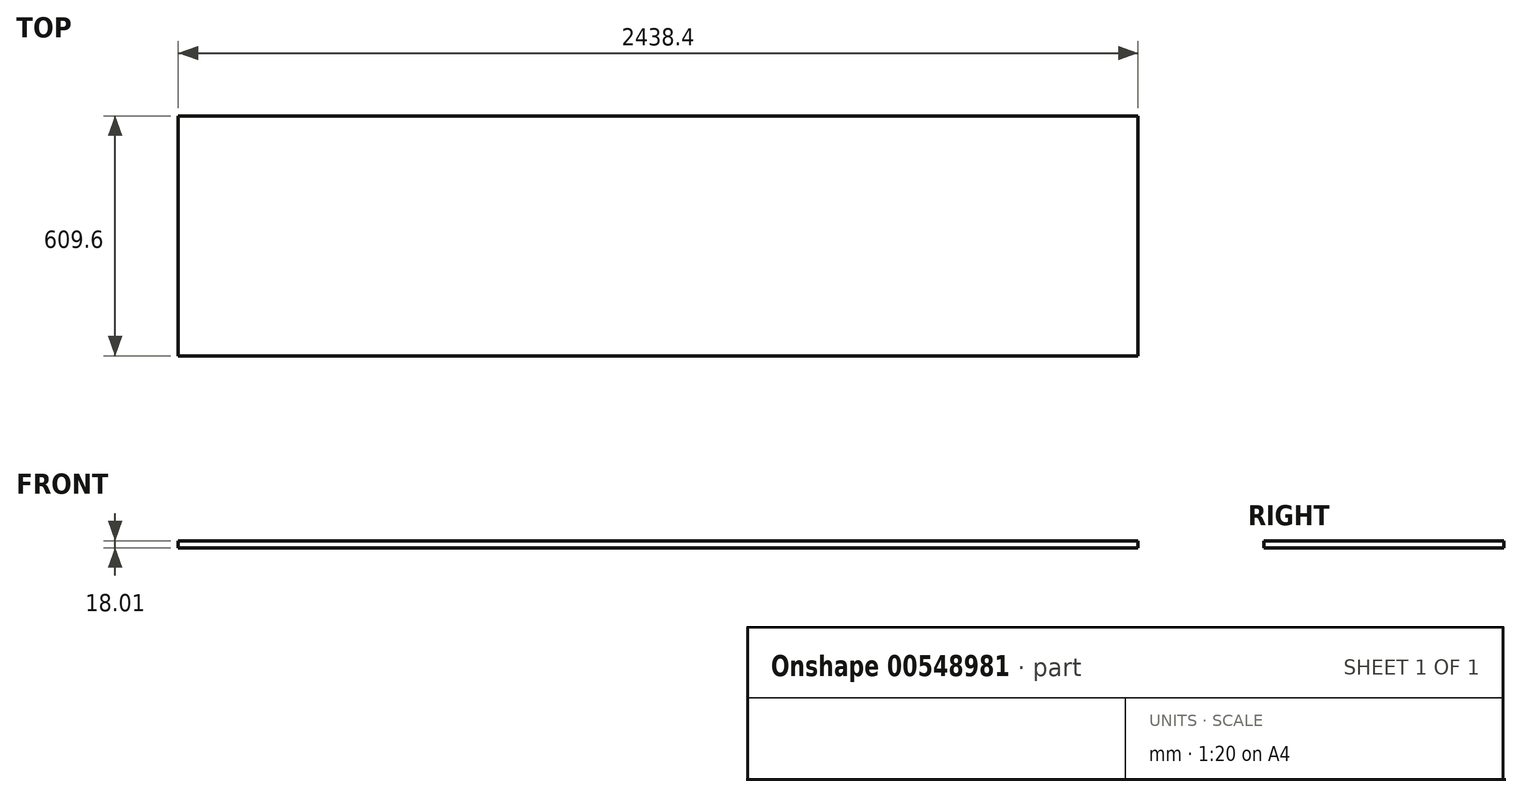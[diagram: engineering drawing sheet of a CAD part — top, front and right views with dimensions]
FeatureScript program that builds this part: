
annotation { "Feature Type Name" : "Feature", "Feature Type Description" : "" }
export const myFeature = defineFeature(function(context is Context, id is Id, definition is map)
    precondition{}
    {
        {
            var Q0;
            Q0=qCreatedBy(makeId("Top.planeOp"),FACE);
            var sketch = newSketch(context, id + "F0", { "sketchPlane" : qUnion([Q0])});
            skLineSegment(sketch, "E0.bottom", {"start": v(1219.2, 304.8) * mm, "end": v(-1219.2, 304.8) * mm});
            skLineSegment(sketch, "E0.top", {"start": v(1219.2, -304.8) * mm, "end": v(-1219.2, -304.8) * mm});
            skLineSegment(sketch, "E0.left", {"start": v(1219.2, 304.8) * mm, "end": v(1219.2, -304.8) * mm});
            skLineSegment(sketch, "E0.right", {"start": v(-1219.2, 304.8) * mm, "end": v(-1219.2, -304.8) * mm});
            skPoint(sketch, "E0.middle", {"position": v(0, 0) * mm});
            skSolve(sketch);
        }
        {
            var Q0;
            Q0 = qSketchRegion(id + "F0", true);
            extrude(context, id + "F1", {"entities" : qUnion([Q0]), "depth" : 18 * mm, "offsetDistance" : 25.4 * mm});
        }
    });
